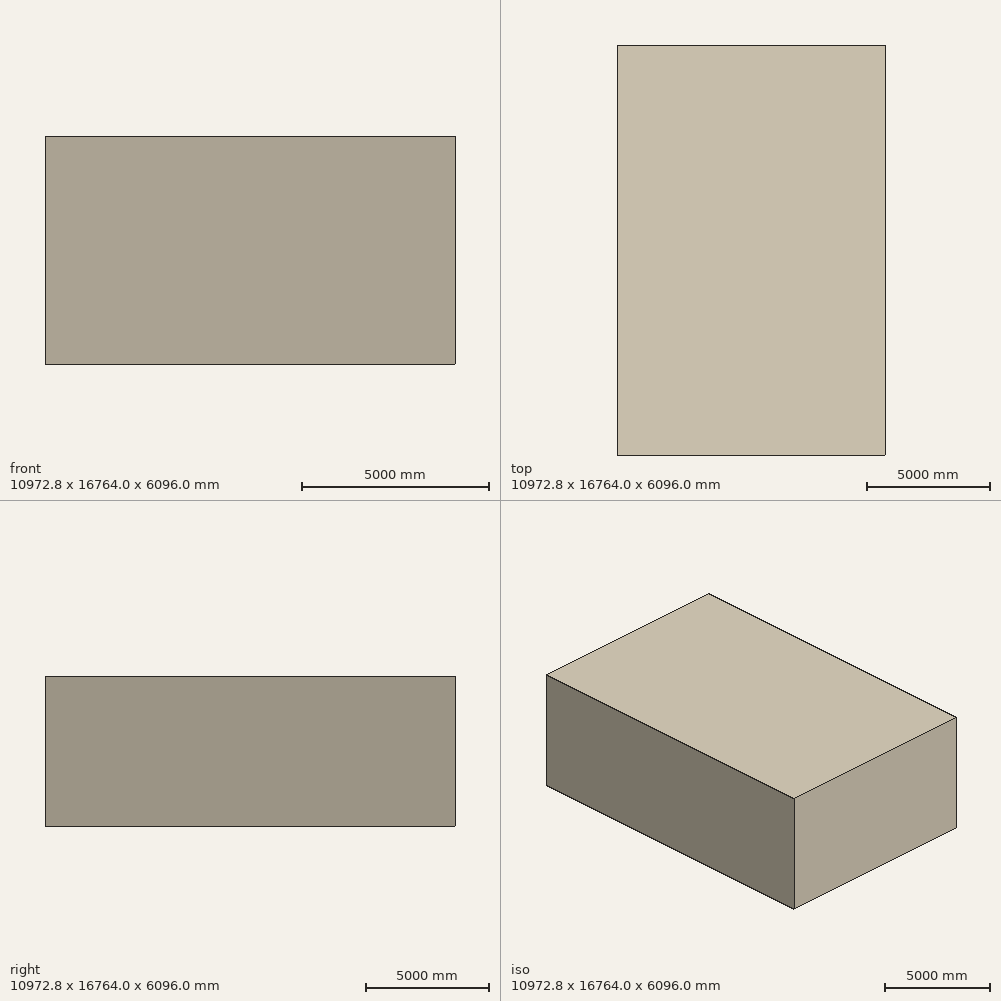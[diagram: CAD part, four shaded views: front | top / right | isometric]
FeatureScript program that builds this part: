
annotation { "Feature Type Name" : "Feature", "Feature Type Description" : "" }
export const myFeature = defineFeature(function(context is Context, id is Id, definition is map)
    precondition{}
    {
        {
            var Q0;
            Q0=qCreatedBy(makeId("Top.planeOp"),FACE);
            var sketch = newSketch(context, id + "F0", { "sketchPlane" : qUnion([Q0])});
            skLineSegment(sketch, "E0.bottom", {"start": v(-5486.4, 8382) * mm, "end": v(5486.4, 8382) * mm});
            skLineSegment(sketch, "E0.top", {"start": v(-5486.4, -8382) * mm, "end": v(5486.4, -8382) * mm});
            skLineSegment(sketch, "E0.left", {"start": v(-5486.4, 8382) * mm, "end": v(-5486.4, -8382) * mm});
            skLineSegment(sketch, "E0.right", {"start": v(5486.4, 8382) * mm, "end": v(5486.4, -8382) * mm});
            skPoint(sketch, "E0.middle", {"position": v(0, 0) * mm});
            skSolve(sketch);
        }
        {
            var Q0;
            Q0 = qSketchRegion(id + "F0", true);
            extrude(context, id + "F1", {"entities" : qUnion([Q0]), "oppositeDirection" : true, "depth" : 6096 * mm, "offsetDistance" : 30.48 * mm});
        }
    });
